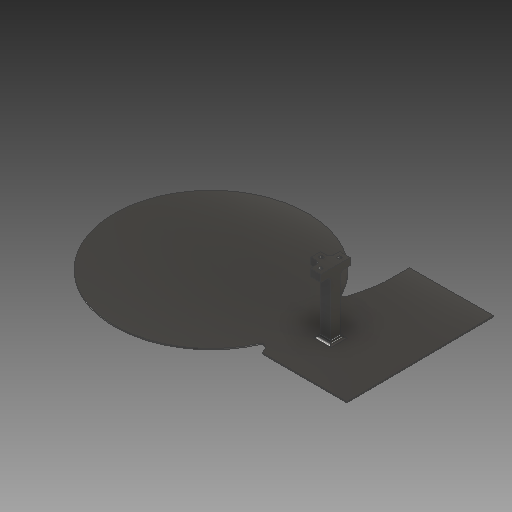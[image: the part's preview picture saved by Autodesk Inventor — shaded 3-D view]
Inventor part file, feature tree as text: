
AUTODESK INVENTOR PART (.ipt)
format: ipt  version: 2018 (Build 220112000, 112)  size: 201,216 bytes
history: native  units: mm
features: sketch x6, other x3
ambient origin geometry x8: Origin, YZ Plane, XZ Plane, XY Plane, X Axis, Y Axis, Z Axis, Center Point
bodies: Volumenkörper1 (feature_tree)
feature tree (9):
  other  "SolarpanelHalterung.ipt"
  other  "Volumenkörper1::SolarpanelHalterung.ipt"
  other  "Bezeichnung1"
  sketch  "Skizze1"  dims[d0=10.0mm]
  sketch  "Skizze2"
  sketch  "Skizze3"
  sketch  "Skizze4"
  sketch  "Skizze5"
  sketch  "Skizze6"
